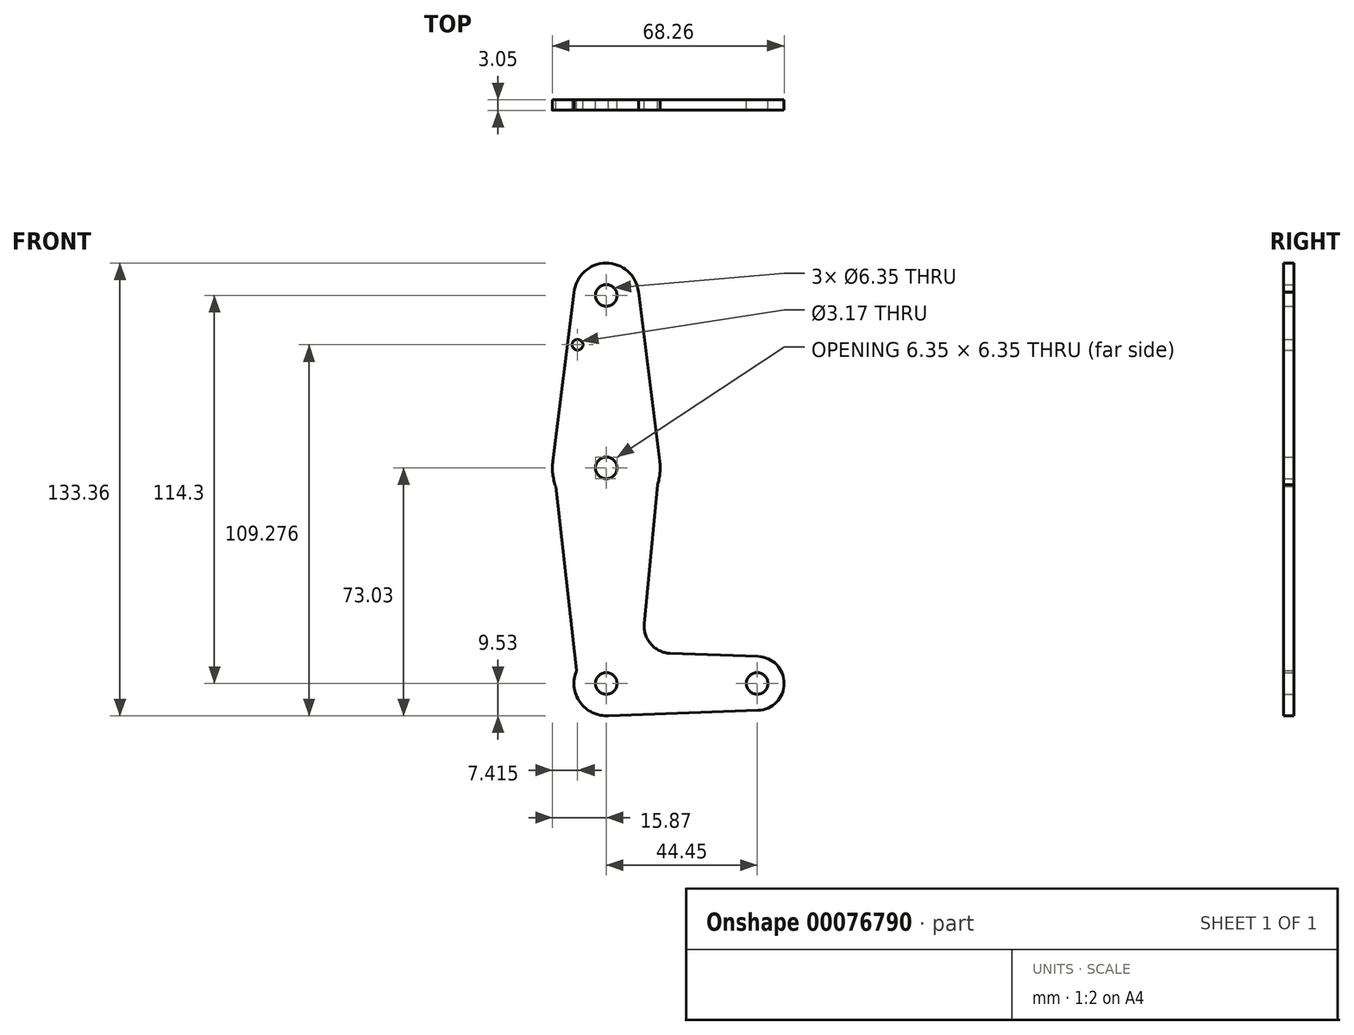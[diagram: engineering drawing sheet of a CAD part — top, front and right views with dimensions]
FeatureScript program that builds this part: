
annotation { "Feature Type Name" : "Feature", "Feature Type Description" : "" }
export const myFeature = defineFeature(function(context is Context, id is Id, definition is map)
    precondition{}
    {
        {
            var Q0;
            Q0=qCreatedBy(makeId("Front.planeOp"),FACE);
            var sketch = newSketch(context, id + "F0", { "sketchPlane" : qUnion([Q0])});
            skCircle(sketch, "E0", {"center": v(0, 114.3) * mm, "radius": 9.53 * mm});
            skLineSegment(sketch, "E1", {"start": v(0, 0) * mm, "end": v(44.45, 0) * mm});
            skCircle(sketch, "E2", {"center": v(0, 63.5) * mm, "radius": 15.88 * mm});
            skCircle(sketch, "E3", {"center": v(0, 0) * mm, "radius": 9.53 * mm});
            skCircle(sketch, "E4", {"center": v(44.45, 0) * mm, "radius": 7.94 * mm});
            skLineSegment(sketch, "E5", {"start": v(0, 114.3) * mm, "end": v(0, 0) * mm});
            skLineSegment(sketch, "E6", {"start": v(-9.4, 115.88) * mm, "end": v(-15.75, 65.49) * mm});
            skLineSegment(sketch, "E7", {"start": v(-15.75, 65.49) * mm, "end": v(-8.71, 3.85) * mm});
            skLineSegment(sketch, "E8", {"start": v(15.75, 65.52) * mm, "end": v(11.22, 17.55) * mm});
            skLineSegment(sketch, "E9", {"start": v(18.85, 8.85) * mm, "end": v(44.73, 7.93) * mm});
            skLineSegment(sketch, "E10", {"start": v(0, -9.53) * mm, "end": v(44.73, -7.93) * mm});
            skLineSegment(sketch, "E11", {"start": v(9.47, 115.35) * mm, "end": v(15.75, 65.52) * mm});
            skArc(sketch, "E12.filletArc", {"start": v(11.22, 17.55) * mm, "mid": v(13.16, 11.55) * mm, "end": v(18.85, 8.85) * mm});
            skCircle(sketch, "E13", {"center": v(0, 114.3) * mm, "radius": 3.18 * mm});
            skCircle(sketch, "E14", {"center": v(0, 63.5) * mm, "radius": 3.18 * mm});
            skCircle(sketch, "E15", {"center": v(0, 0) * mm, "radius": 3.18 * mm});
            skCircle(sketch, "E16", {"center": v(44.45, 0) * mm, "radius": 3.18 * mm});
            skCircle(sketch, "E17", {"center": v(-8.45, 99.75) * mm, "radius": 1.59 * mm});
            skSolve(sketch);
        }
        {
            var Q0;
            Q0 = qSketchRegion(id + "F0", true);
            var Q1;
            {var subQ0=sQuery(id+"F0.wireOp",EDGE,"E15");var subQ1=sQuery(id+"F0.wireOp",EDGE,"E1");var subQ2=makeQuery(id+"F0.imprint","INTERSECT",VERTEX,{"derivedFrom":[subQ1,subQ0]});Q1=makeQuery(id+"F0.imprint","IMPRINT",FACE,{"disambiguationData":[TD([[makeQuery(id+"F0.imprint","IMPRINT",EDGE,{"disambiguationData":[TD([[subQ2,-1.0]])],"derivedFrom":subQ1}),1.0]])]});}
            extrude(context, id + "F1", {"entities" : qUnion([Q0, Q1]), "depth" : 3.05 * mm});
        }
    });
